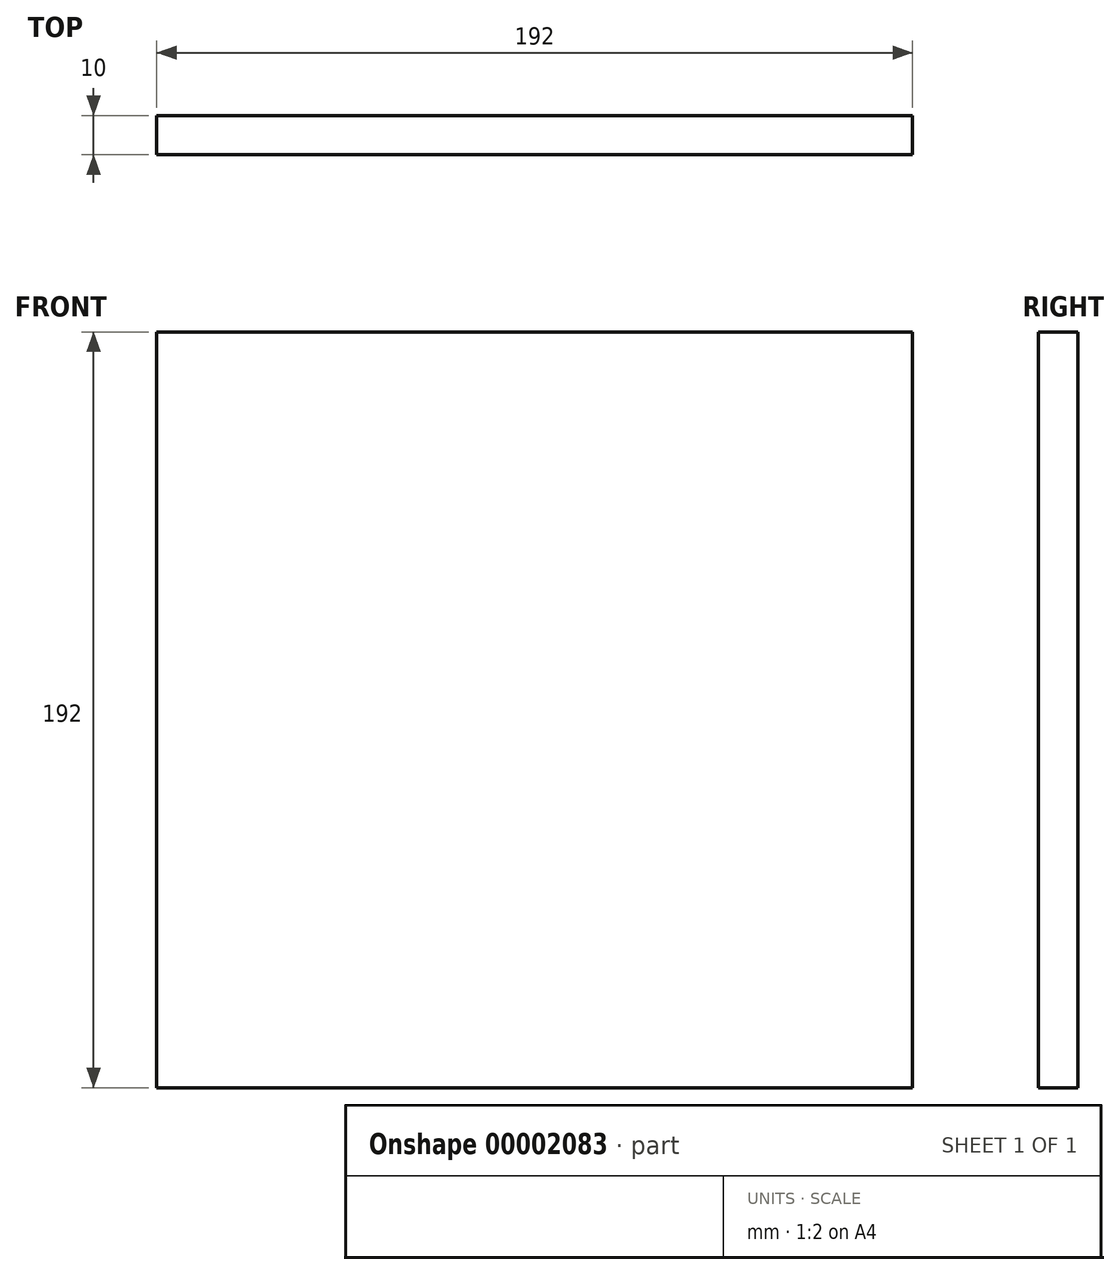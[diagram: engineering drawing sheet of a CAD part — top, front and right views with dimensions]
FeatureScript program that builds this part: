
annotation { "Feature Type Name" : "Feature", "Feature Type Description" : "" }
export const myFeature = defineFeature(function(context is Context, id is Id, definition is map)
    precondition{}
    {
        {
            var Q0;
            Q0=qCreatedBy(makeId("Front.planeOp"),FACE);
            var sketch = newSketch(context, id + "F0", { "sketchPlane" : qUnion([Q0])});
            skLineSegment(sketch, "E0.rect.bottom", {"start": v(96, -96) * mm, "end": v(-96, -96) * mm});
            skLineSegment(sketch, "E0.rect.top", {"start": v(96, 96) * mm, "end": v(-96, 96) * mm});
            skLineSegment(sketch, "E0.rect.left", {"start": v(96, -96) * mm, "end": v(96, 96) * mm});
            skLineSegment(sketch, "E0.rect.right", {"start": v(-96, -96) * mm, "end": v(-96, 96) * mm});
            skPoint(sketch, "E0.rect.middle", {"position": v(0, 0) * mm});
            skSolve(sketch);
        }
        {
            var Q0;
            Q0 = qSketchRegion(id + "F0", true);
            extrude(context, id + "F1", {"entities" : qUnion([Q0]), "depth" : 10 * mm});
        }
    });
